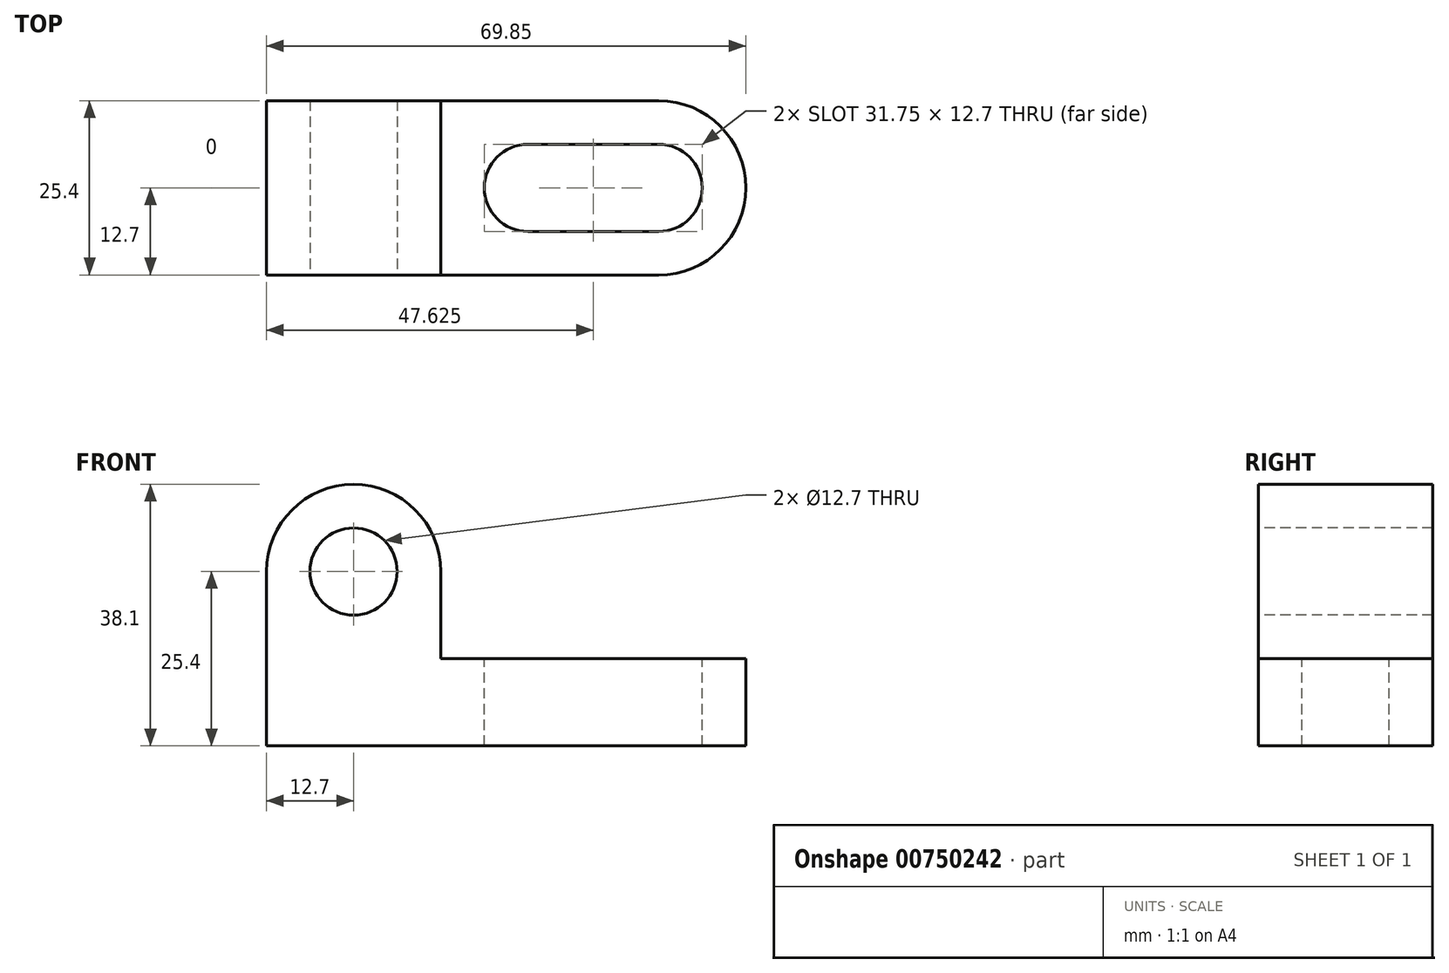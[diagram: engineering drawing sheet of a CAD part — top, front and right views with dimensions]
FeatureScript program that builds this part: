
annotation { "Feature Type Name" : "Feature", "Feature Type Description" : "" }
export const myFeature = defineFeature(function(context is Context, id is Id, definition is map)
    precondition{}
    {
        {
            var Q0;
            Q0=qCreatedBy(makeId("Front.planeOp"),FACE);
            var sketch = newSketch(context, id + "F0", { "sketchPlane" : qUnion([Q0])});
            skLineSegment(sketch, "E0", {"start": v(0, 0) * mm, "end": v(0, 38.1) * mm});
            skLineSegment(sketch, "E1", {"start": v(0, 38.1) * mm, "end": v(69.85, 38.1) * mm});
            skLineSegment(sketch, "E2", {"start": v(69.85, 38.1) * mm, "end": v(69.85, 0) * mm});
            skLineSegment(sketch, "E3", {"start": v(69.85, 0) * mm, "end": v(0, 0) * mm});
            skSolve(sketch);
        }
        {
            var Q0;
            Q0=makeQuery(id+"F0.imprint","IMPRINT",FACE,{"disambiguationData":[TD([[makeQuery(id+"F0.imprint","IMPRINT",EDGE,{"derivedFrom":sQuery(id+"F0.wireOp",EDGE,"E0")}),-1.0]])]});
            extrude(context, id + "F1", {"entities" : qUnion([Q0]), "depth" : 25.4 * mm, "offsetDistance" : 25.4 * mm});
        }
        {
            var Q0;
            Q0=makeQuery(id+"F1.opExtrude","CAP_FACE",FACE,{"disambiguationData":[OSD([sQuery(id+"F0.wireOp",EDGE,"E0"),sQuery(id+"F0.wireOp",EDGE,"E1"),sQuery(id+"F0.wireOp",EDGE,"E2"),sQuery(id+"F0.wireOp",EDGE,"E3")])],"isStart":false});
            var sketch = newSketch(context, id + "F2", { "sketchPlane" : qUnion([Q0])});
            skLineSegment(sketch, "E4", {"start": v(25.4, 38.1) * mm, "end": v(25.4, 12.7) * mm});
            skLineSegment(sketch, "E5", {"start": v(25.4, 12.7) * mm, "end": v(69.85, 12.7) * mm});
            skLineSegment(sketch, "E6", {"start": v(69.85, 12.7) * mm, "end": v(69.85, 38.1) * mm});
            skLineSegment(sketch, "E7", {"start": v(69.85, 38.1) * mm, "end": v(25.4, 38.1) * mm});
            skSolve(sketch);
        }
        {
            var Q0;
            Q0=makeQuery(id+"F2.imprint","IMPRINT",FACE,{"disambiguationData":[TD([[makeQuery(id+"F2.imprint","IMPRINT",EDGE,{"derivedFrom":sQuery(id+"F2.wireOp",EDGE,"E4")}),1.0]])]});
            extrude(context, id + "F3", {"entities" : qUnion([Q0]), "operationType" : NewBodyOperationType.REMOVE, "oppositeDirection" : true, "depth" : 25.4 * mm, "offsetDistance" : 25.4 * mm});
        }
        {
            var Q0;
            Q0=makeQuery(id+"F3.boolean.opBoolean","COPY",FACE,{"derivedFrom":makeQuery(id+"F3.opExtrude","SWEPT_FACE",FACE,{"disambiguationData":[OSD([sQuery(id+"F2.wireOp",EDGE,"E5")])]})});
            var sketch = newSketch(context, id + "F4", { "sketchPlane" : qUnion([Q0])});
            skArc(sketch, "E8", {"start": v(57.15, -25.4) * mm, "mid": v(69.85, -12.7) * mm, "end": v(57.15, 0) * mm});
            skSolve(sketch);
        }
        {
            var Q0;
            {var subQ0=sQuery(id+"F4.wireOp",EDGE,"E8");var subQ1=sQuery(id+"F2.wireOp",EDGE,"E5");var subQ2=makeQuery(id+"F3.boolean.opBoolean","COPY",EDGE,{"derivedFrom":makeQuery(id+"F3.opExtrude","CAP_EDGE",EDGE,{"disambiguationData":[OSD([subQ1])],"isStart":false})});var subQ3=makeQuery(id+"F4.imprint","INTERSECT",VERTEX,{"derivedFrom":[subQ2,subQ0]});Q0=makeQuery(id+"F4.imprint","IMPRINT",FACE,{"disambiguationData":[TD([[makeQuery(id+"F4.imprint","IMPRINT",EDGE,{"disambiguationData":[TD([[subQ3,1.0]])],"derivedFrom":subQ0}),-1.0]])]});}
            var Q1;
            {var subQ0=sQuery(id+"F4.wireOp",EDGE,"E8");var subQ1=sQuery(id+"F2.wireOp",EDGE,"E5");var subQ2=makeQuery(id+"F3.boolean.opBoolean","COPY",EDGE,{"derivedFrom":makeQuery(id+"F3.opExtrude","CAP_EDGE",EDGE,{"disambiguationData":[OSD([subQ1])],"isStart":true})});var subQ3=makeQuery(id+"F4.imprint","INTERSECT",VERTEX,{"derivedFrom":[subQ2,subQ0]});Q1=makeQuery(id+"F4.imprint","IMPRINT",FACE,{"disambiguationData":[TD([[makeQuery(id+"F4.imprint","IMPRINT",EDGE,{"disambiguationData":[TD([[subQ3,-1.0]])],"derivedFrom":subQ0}),-1.0]])]});}
            extrude(context, id + "F5", {"entities" : qUnion([Q0, Q1]), "operationType" : NewBodyOperationType.REMOVE, "oppositeDirection" : true, "depth" : 12.7 * mm, "offsetDistance" : 25.4 * mm});
        }
        {
            var Q0;
            Q0=makeQuery(id+"F1.opExtrude","CAP_FACE",FACE,{"disambiguationData":[OSD([sQuery(id+"F0.wireOp",EDGE,"E0"),sQuery(id+"F0.wireOp",EDGE,"E1"),sQuery(id+"F0.wireOp",EDGE,"E2"),sQuery(id+"F0.wireOp",EDGE,"E3")])],"isStart":false});
            var sketch = newSketch(context, id + "F6", { "sketchPlane" : qUnion([Q0])});
            skArc(sketch, "E9", {"start": v(25.4, 25.4) * mm, "mid": v(12.7, 38.1) * mm, "end": v(0, 25.4) * mm});
            skSolve(sketch);
        }
        {
            var Q0;
            {var subQ0=sQuery(id+"F6.wireOp",EDGE,"E9");var subQ1=makeQuery(id+"F1.opExtrude","CAP_EDGE",EDGE,{"disambiguationData":[OSD([sQuery(id+"F0.wireOp",EDGE,"E1")])],"isStart":false});var subQ2=makeQuery(id+"F6.imprint","INTERSECT",VERTEX,{"derivedFrom":[subQ1,subQ0]});Q0=makeQuery(id+"F6.imprint","IMPRINT",FACE,{"disambiguationData":[TD([[makeQuery(id+"F6.imprint","IMPRINT",EDGE,{"disambiguationData":[TD([[subQ2,-1.0]])],"derivedFrom":subQ0}),-1.0]])]});}
            var Q1;
            {var subQ0=sQuery(id+"F6.wireOp",EDGE,"E9");var subQ1=makeQuery(id+"F1.opExtrude","CAP_EDGE",EDGE,{"disambiguationData":[OSD([sQuery(id+"F0.wireOp",EDGE,"E1")])],"isStart":false});var subQ2=makeQuery(id+"F6.imprint","INTERSECT",VERTEX,{"derivedFrom":[subQ1,subQ0]});Q1=makeQuery(id+"F6.imprint","IMPRINT",FACE,{"disambiguationData":[TD([[makeQuery(id+"F6.imprint","IMPRINT",EDGE,{"disambiguationData":[TD([[subQ2,1.0]])],"derivedFrom":subQ0}),-1.0]])]});}
            extrude(context, id + "F7", {"entities" : qUnion([Q0, Q1]), "operationType" : NewBodyOperationType.REMOVE, "oppositeDirection" : true, "depth" : 25.4 * mm, "offsetDistance" : 25.4 * mm});
        }
        {
            var Q0;
            Q0=makeQuery(id+"F3.boolean.opBoolean","COPY",FACE,{"derivedFrom":makeQuery(id+"F3.opExtrude","SWEPT_FACE",FACE,{"disambiguationData":[OSD([sQuery(id+"F2.wireOp",EDGE,"E5")])]})});
            var sketch = newSketch(context, id + "F8", { "sketchPlane" : qUnion([Q0])});
            skCircle(sketch, "E10", {"center": v(38.1, -12.7) * mm, "radius": 6.35 * mm});
            skCircle(sketch, "E11", {"center": v(57.15, -12.7) * mm, "radius": 6.35 * mm});
            skLineSegment(sketch, "E12", {"start": v(38.1, -12.7) * mm, "end": v(38.1, -19.05) * mm});
            skLineSegment(sketch, "E13", {"start": v(38.1, -19.05) * mm, "end": v(57.15, -19.05) * mm});
            skLineSegment(sketch, "E14", {"start": v(57.15, -19.05) * mm, "end": v(57.15, -12.7) * mm});
            skLineSegment(sketch, "E15", {"start": v(57.15, -6.35) * mm, "end": v(38.1, -6.35) * mm});
            skLineSegment(sketch, "E16", {"start": v(38.1, -6.35) * mm, "end": v(38.1, -12.7) * mm});
            skSolve(sketch);
        }
        {
            var Q0;
            {var subQ0=sQuery(id+"F8.wireOp",EDGE,"E12");Q0=makeQuery(id+"F8.imprint","IMPRINT",FACE,{"disambiguationData":[TD([[makeQuery(id+"F8.imprint","IMPRINT",EDGE,{"derivedFrom":subQ0}),-1.0]])]});}
            var Q1;
            {var subQ0=sQuery(id+"F8.wireOp",EDGE,"E13");Q1=makeQuery(id+"F8.imprint","IMPRINT",FACE,{"disambiguationData":[TD([[makeQuery(id+"F8.imprint","IMPRINT",EDGE,{"derivedFrom":subQ0}),1.0]])]});}
            var Q2;
            {var subQ0=sQuery(id+"F8.wireOp",EDGE,"E12");Q2=makeQuery(id+"F8.imprint","IMPRINT",FACE,{"disambiguationData":[TD([[makeQuery(id+"F8.imprint","IMPRINT",EDGE,{"derivedFrom":subQ0}),1.0]])]});}
            var Q3;
            {var subQ0=sQuery(id+"F8.wireOp",EDGE,"E11");var subQ1=makeQuery(id+"F8.imprint","INTERSECT",VERTEX,{"derivedFrom":[subQ0,sQuery(id+"F8.wireOp",EDGE,"E13")]});Q3=makeQuery(id+"F8.imprint","IMPRINT",FACE,{"disambiguationData":[TD([[makeQuery(id+"F8.imprint","IMPRINT",EDGE,{"disambiguationData":[TD([[subQ1,1.0]])],"derivedFrom":subQ0}),1.0]])]});}
            extrude(context, id + "F9", {"entities" : qUnion([Q0, Q1, Q2, Q3]), "operationType" : NewBodyOperationType.REMOVE, "oppositeDirection" : true, "depth" : 12.7 * mm, "offsetDistance" : 25.4 * mm});
        }
        {
            var Q0;
            Q0=makeQuery(id+"F1.opExtrude","CAP_FACE",FACE,{"disambiguationData":[OSD([sQuery(id+"F0.wireOp",EDGE,"E0"),sQuery(id+"F0.wireOp",EDGE,"E1"),sQuery(id+"F0.wireOp",EDGE,"E2"),sQuery(id+"F0.wireOp",EDGE,"E3")])],"isStart":false});
            var sketch = newSketch(context, id + "F10", { "sketchPlane" : qUnion([Q0])});
            skCircle(sketch, "E17", {"center": v(12.7, 25.4) * mm, "radius": 6.35 * mm});
            skSolve(sketch);
        }
        {
            var Q0;
            Q0=makeQuery(id+"F10.imprint","IMPRINT",FACE,{"disambiguationData":[TD([[makeQuery(id+"F10.imprint","IMPRINT",EDGE,{"derivedFrom":sQuery(id+"F10.wireOp",EDGE,"E17")}),1.0]])]});
            extrude(context, id + "F11", {"entities" : qUnion([Q0]), "operationType" : NewBodyOperationType.REMOVE, "oppositeDirection" : true, "depth" : 25.4 * mm, "offsetDistance" : 25.4 * mm});
        }
    });
